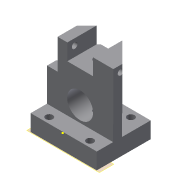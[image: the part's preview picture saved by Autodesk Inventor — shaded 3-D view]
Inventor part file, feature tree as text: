
AUTODESK INVENTOR PART (.ipt)
format: ipt  version: 2019.4 (Build 234330000, 330)  size: 190,464 bytes
history: native  units: mm
features: reference x11, sketch x7, other x7, extrude x6, plane x3, projected_geometry x2
ambient origin geometry x8: Origin, YZ Plane, XZ Plane, XY Plane, X Axis, Y Axis, Z Axis, Center Point
bodies: Body1 (feature_tree)
feature tree (36):
  plane  "Work Plane5"
  extrude  "Extrusion4"  TaperAngle=45.0deg  [1 undecoded]
  sketch  "Sketch7"  dims[d26=45.0deg d27=3.0mm]
  sketch  "Sketch8"  dims[d28=11.0mm d29=11.0mm]
  plane  "Work Plane7"
  extrude  "Extrusion5"  Depth=3.0mm
  sketch  "Sketch9"  dims[d30=8.0mm d31=10.0mm d32=0.0mm]
  plane  "Work Plane8"
  extrude  "Extrusion6"  Depth=11.0mm
  extrude  "Extrusion7"  Depth=10.0mm TaperAngle=0.0deg
  extrude  "Extrusion8"  Depth=0.3mm
  extrude  "Extrusion9"  Depth=10.0mm
  sketch  "Sketch5"  dims[d18=8.0mm d19=0.0mm d25=45.0deg]
  reference  "Reference18"
  reference  "Reference19"
  reference  "Reference20"
  reference  "Reference21"
  projected_geometry  "Projected Loop3"
  reference  "Reference23"
  reference  "Reference24"
  reference  "Reference25"
  reference  "Reference26"
  sketch  "Sketch10"  dims[d34=0.3mm d35=0.3mm]
  projected_geometry  "Projected Loop4"
  sketch  "Sketch11"  dims[d36=10.0mm d37=0.0mm d38=2.8mm]
  reference  "Reference27"
  sketch  "Sketch12"  dims[d39=10.0mm d40=0.0mm d41=0.7mm d42=10.0mm d43=0.0mm d44=0.0mm d45=0.0mm d46=2.8mm]
  reference  "Reference28"
  reference  "Reference29"
  other  "Assembly_opentrons_microscope_slide_y.iam"
  other  "00_MGN12H, LINEAR GUIDE BLOCK:2"
  other  "00_MGN12 LINEAR GUIDE RAIL, CONFIGURABLE:1"
  other  "Assembly_Opentrons_Imagingunit_v3.iam"
  other  "Assembly_Opentrons_Autofocus_v2:1"
  other  "01_Slide_camera_v1:1"
  other  "06_Fluorescence_Arm:1"
note: 1 required parameter value undecoded (feature->parameter linkage not recoverable at this tier; creation-order binding heuristic only, values carry confidence <= 0.55)
